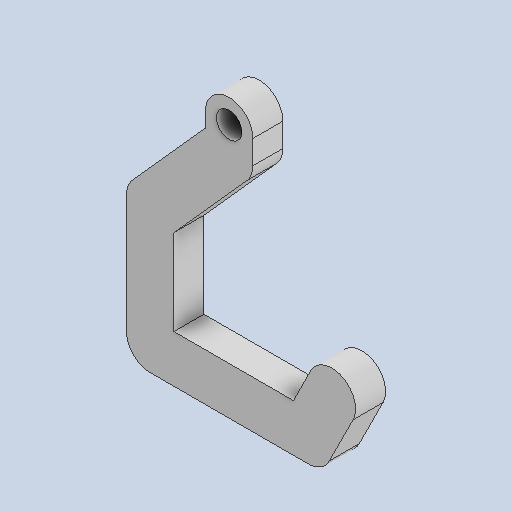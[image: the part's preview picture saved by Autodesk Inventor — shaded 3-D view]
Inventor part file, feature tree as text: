
AUTODESK INVENTOR PART (.ipt)
format: ipt  version: 2025.2 (Build 292293000, 293)  size: 133,120 bytes
history: native  units: mm
features: extrude x1, sketch x1
ambient origin geometry x8: Origin, YZ Plane, XZ Plane, XY Plane, X Axis, Y Axis, Z Axis, Center Point
bodies: Solid1 (feature_tree)
feature tree (2):
  extrude  "Extrusion1"  Depth=6.0mm
  sketch  "Sketch1"  dims[d0=3.2mm d1=6.0mm d2=3.0mm d3=6.0mm d4=6.0mm d5=6.0mm d6=6.0mm d7=15.0mm d8=6.0mm d9=15.0mm d10=20.0mm d11=3.0mm d12=6.0mm d13=3.8mm d14=0.0mm d15=1.0mm d16=1.0mm d17=1.0mm d18=0.15mm d19=0.25mm d20=0.375mm d21=14.3117mm d22=0.75mm d23=20.594885mm d24=0.0625mm d25=0.75mm d26=0.375mm]
